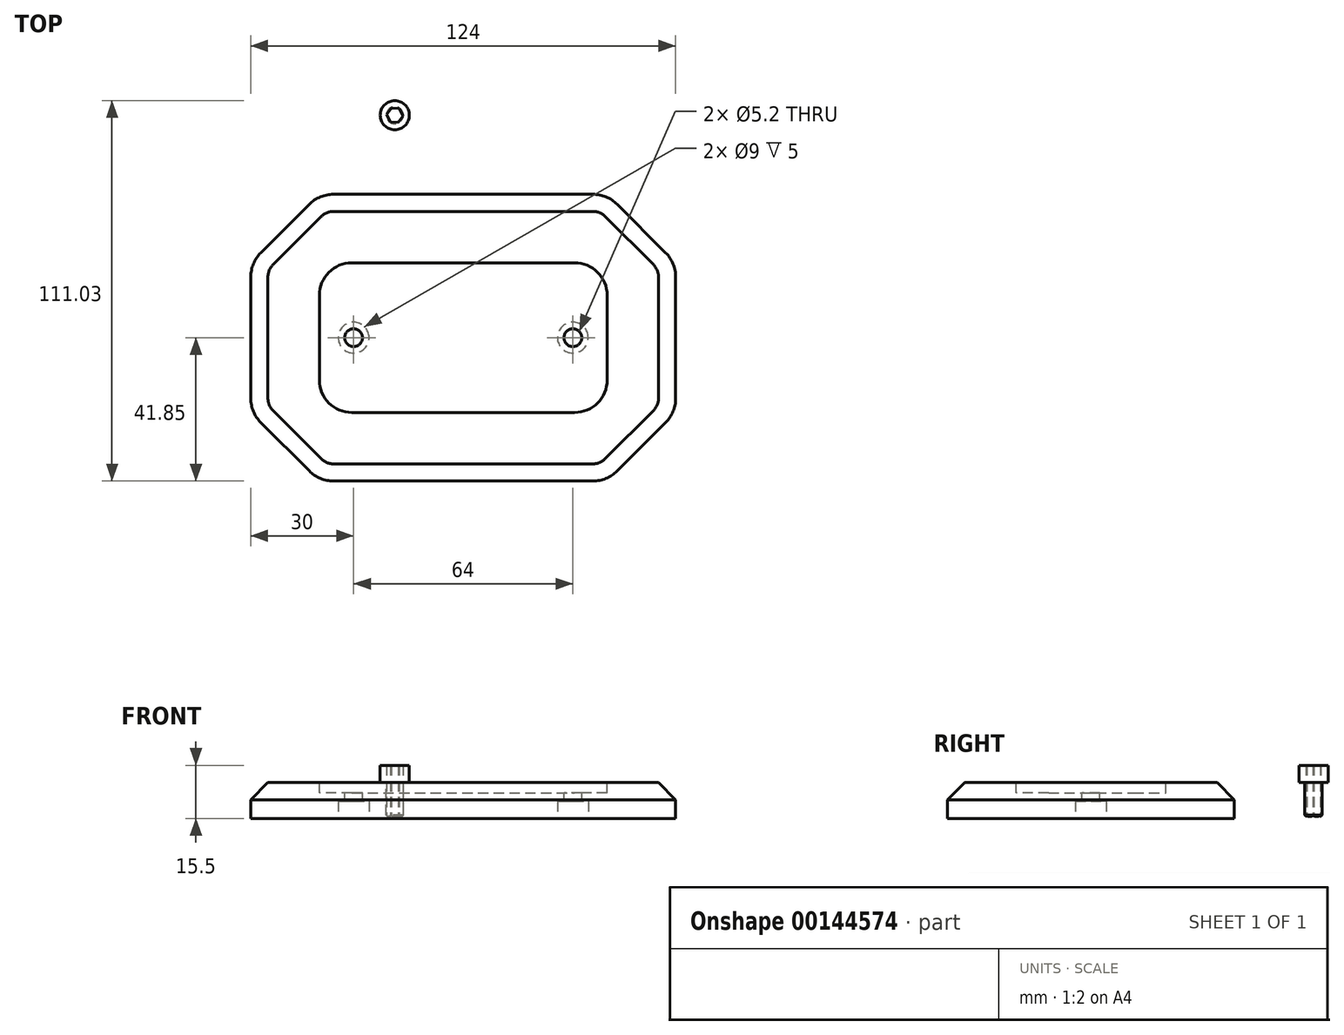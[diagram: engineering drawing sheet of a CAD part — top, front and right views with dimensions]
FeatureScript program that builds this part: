
annotation { "Feature Type Name" : "Feature", "Feature Type Description" : "" }
export const myFeature = defineFeature(function(context is Context, id is Id, definition is map)
    precondition{}
    {
        {
            var Q0;
            Q0=qCreatedBy(makeId("Top.planeOp"),FACE);
            var sketch = newSketch(context, id + "F0", { "sketchPlane" : qUnion([Q0])});
            skLineSegment(sketch, "E0.bottom", {"start": v(9.5, -43.7) * mm, "end": v(74.5, -43.7) * mm});
            skLineSegment(sketch, "E0.top", {"start": v(9.5, 0) * mm, "end": v(74.5, 0) * mm});
            skLineSegment(sketch, "E0.left", {"start": v(0, -34.2) * mm, "end": v(0, -9.5) * mm});
            skLineSegment(sketch, "E0.right", {"start": v(84, -34.2) * mm, "end": v(84, -9.5) * mm});
            skPoint(sketch, "E1.visualSharp", {"position": v(0, 0) * mm});
            skArc(sketch, "E1.filletArc", {"start": v(9.5, 0) * mm, "mid": v(2.78, -2.78) * mm, "end": v(0, -9.5) * mm});
            skPoint(sketch, "E2.visualSharp", {"position": v(84, 0) * mm});
            skArc(sketch, "E2.filletArc", {"start": v(84, -9.5) * mm, "mid": v(81.22, -2.78) * mm, "end": v(74.5, 0) * mm});
            skPoint(sketch, "E3.visualSharp", {"position": v(84, -43.7) * mm});
            skArc(sketch, "E3.filletArc", {"start": v(74.5, -43.7) * mm, "mid": v(81.22, -40.92) * mm, "end": v(84, -34.2) * mm});
            skPoint(sketch, "E4.visualSharp", {"position": v(0, -43.7) * mm});
            skArc(sketch, "E4.filletArc", {"start": v(0, -34.2) * mm, "mid": v(2.78, -40.92) * mm, "end": v(9.5, -43.7) * mm});
            skLineSegment(sketch, "E5.bottom", {"start": v(-20, 20) * mm, "end": v(104, 20) * mm, "construction": true});
            skLineSegment(sketch, "E5.top", {"start": v(-20, -63.7) * mm, "end": v(104, -63.7) * mm, "construction": true});
            skLineSegment(sketch, "E5.left", {"start": v(-20, 20) * mm, "end": v(-20, -63.7) * mm, "construction": true});
            skLineSegment(sketch, "E5.right", {"start": v(104, 20) * mm, "end": v(104, -63.7) * mm, "construction": true});
            skLineSegment(sketch, "E6", {"start": v(0, 20) * mm, "end": v(84, 20) * mm});
            skLineSegment(sketch, "E7", {"start": v(-20, 0) * mm, "end": v(-20, -43.7) * mm});
            skLineSegment(sketch, "E8", {"start": v(-20, 0) * mm, "end": v(0, 20) * mm});
            skLineSegment(sketch, "E9", {"start": v(84, 20) * mm, "end": v(104, 0) * mm});
            skLineSegment(sketch, "E10", {"start": v(104, 0) * mm, "end": v(104, -43.7) * mm});
            skLineSegment(sketch, "E11", {"start": v(104, -43.7) * mm, "end": v(84, -63.7) * mm});
            skLineSegment(sketch, "E12", {"start": v(84, -63.7) * mm, "end": v(0, -63.7) * mm});
            skLineSegment(sketch, "E13", {"start": v(0, -63.7) * mm, "end": v(-20, -43.7) * mm});
            skCircle(sketch, "E14", {"center": v(74, -21.85) * mm, "radius": 2.6 * mm});
            skLineSegment(sketch, "E15", {"start": v(84, -21.85) * mm, "end": v(0, -21.85) * mm, "construction": true});
            skCircle(sketch, "E16", {"center": v(10, -21.85) * mm, "radius": 2.6 * mm});
            skCircle(sketch, "E17", {"center": v(22.02, 43.08) * mm, "radius": 4.25 * mm});
            skCircle(sketch, "E18", {"center": v(22.02, 43.08) * mm, "radius": 2.5 * mm});
            skCircle(sketch, "E19.cCircle", {"center": v(22.02, 43.08) * mm, "radius": 2.07 * mm, "construction": true});
            skLineSegment(sketch, "E19.0", {"start": v(23.34, 45.06) * mm, "end": v(24.4, 42.92) * mm});
            skLineSegment(sketch, "E19.1", {"start": v(24.4, 42.92) * mm, "end": v(23.07, 40.94) * mm});
            skLineSegment(sketch, "E19.2", {"start": v(23.07, 40.94) * mm, "end": v(20.7, 41.1) * mm});
            skLineSegment(sketch, "E19.3", {"start": v(20.7, 41.1) * mm, "end": v(19.64, 43.23) * mm});
            skLineSegment(sketch, "E19.4", {"start": v(19.64, 43.23) * mm, "end": v(20.96, 45.22) * mm});
            skLineSegment(sketch, "E19.5", {"start": v(20.96, 45.22) * mm, "end": v(23.34, 45.06) * mm});
            skPoint(sketch, "E19.0.midPoint", {"position": v(23.87, 44) * mm});
            skSolve(sketch);
        }
        {
            var Q0;
            Q0=makeQuery(id+"F0.imprint","IMPRINT",FACE,{"disambiguationData":[TD([[makeQuery(id+"F0.imprint","IMPRINT",EDGE,{"derivedFrom":sQuery(id+"F0.wireOp",EDGE,"E0.bottom")}),1.0]])]});
            var Q1;
            Q1=makeQuery(id+"F0.imprint","IMPRINT",FACE,{"disambiguationData":[TD([[makeQuery(id+"F0.imprint","IMPRINT",EDGE,{"derivedFrom":sQuery(id+"F0.wireOp",EDGE,"E0.bottom")}),-1.0]])]});
            extrude(context, id + "F1", {"entities" : qUnion([Q0, Q1]), "oppositeDirection" : true, "depth" : 10.5 * mm});
        }
        {
            var Q0;
            Q0=makeQuery(id+"F0.imprint","IMPRINT",FACE,{"disambiguationData":[TD([[makeQuery(id+"F0.imprint","IMPRINT",EDGE,{"derivedFrom":sQuery(id+"F0.wireOp",EDGE,"E0.bottom")}),1.0]])]});
            extrude(context, id + "F2", {"entities" : qUnion([Q0]), "operationType" : NewBodyOperationType.REMOVE, "oppositeDirection" : true, "depth" : 3 * mm});
        }
        {
            var Q0;
            Q0=makeQuery(id+"F1.opExtrude","SWEPT_EDGE",EDGE,{"disambiguationData":[OSD([sQuery(id+"F0.wireOp",EDGE,"E6"),sQuery(id+"F0.wireOp",EDGE,"E8")])]});
            var Q1;
            Q1=makeQuery(id+"F1.opExtrude","SWEPT_EDGE",EDGE,{"disambiguationData":[OSD([sQuery(id+"F0.wireOp",EDGE,"E7"),sQuery(id+"F0.wireOp",EDGE,"E8")])]});
            var Q2;
            Q2=makeQuery(id+"F1.opExtrude","SWEPT_EDGE",EDGE,{"disambiguationData":[OSD([sQuery(id+"F0.wireOp",EDGE,"E7"),sQuery(id+"F0.wireOp",EDGE,"E13")])]});
            var Q3;
            Q3=makeQuery(id+"F1.opExtrude","SWEPT_EDGE",EDGE,{"disambiguationData":[OSD([sQuery(id+"F0.wireOp",EDGE,"E12"),sQuery(id+"F0.wireOp",EDGE,"E13")])]});
            var Q4;
            Q4=makeQuery(id+"F1.opExtrude","SWEPT_EDGE",EDGE,{"disambiguationData":[OSD([sQuery(id+"F0.wireOp",EDGE,"E11"),sQuery(id+"F0.wireOp",EDGE,"E12")])]});
            var Q5;
            Q5=makeQuery(id+"F1.opExtrude","SWEPT_EDGE",EDGE,{"disambiguationData":[OSD([sQuery(id+"F0.wireOp",EDGE,"E10"),sQuery(id+"F0.wireOp",EDGE,"E11")])]});
            var Q6;
            Q6=makeQuery(id+"F1.opExtrude","SWEPT_EDGE",EDGE,{"disambiguationData":[OSD([sQuery(id+"F0.wireOp",EDGE,"E9"),sQuery(id+"F0.wireOp",EDGE,"E10")])]});
            var Q7;
            Q7=makeQuery(id+"F1.opExtrude","SWEPT_EDGE",EDGE,{"disambiguationData":[OSD([sQuery(id+"F0.wireOp",EDGE,"E6"),sQuery(id+"F0.wireOp",EDGE,"E9")])]});
            fillet(context, id + "F3", {"entities" : qUnion([Q0, Q1, Q2, Q3, Q4, Q5, Q6, Q7]), "radius" : 10 * mm, "tangentPropagation" : true, "allowEdgeOverflow" : false});
        }
        {
            var Q0;
            Q0=makeQuery(id+"F1.opExtrude","CAP_EDGE",EDGE,{"disambiguationData":[OSD([sQuery(id+"F0.wireOp",EDGE,"E12")])],"isStart":true});
            chamfer(context, id + "F4", {"entities" : qUnion([Q0]), "width" : 5 * mm, "tangentPropagation" : true});
        }
        {
            var Q0;
            Q0=makeQuery(id+"F1.opExtrude","CAP_FACE",FACE,{"disambiguationData":[OSD([sQuery(id+"F0.wireOp",EDGE,"E6"),sQuery(id+"F0.wireOp",EDGE,"E7"),sQuery(id+"F0.wireOp",EDGE,"E8"),sQuery(id+"F0.wireOp",EDGE,"E9"),sQuery(id+"F0.wireOp",EDGE,"E10"),sQuery(id+"F0.wireOp",EDGE,"E11"),sQuery(id+"F0.wireOp",EDGE,"E12"),sQuery(id+"F0.wireOp",EDGE,"E13"),sQuery(id+"F0.wireOp",EDGE,"E14"),sQuery(id+"F0.wireOp",EDGE,"E16")])],"isStart":false});
            var sketch = newSketch(context, id + "F5", { "sketchPlane" : qUnion([Q0])});
            skPoint(sketch, "E20.0", {"position": v(74, 21.85) * mm});
            skPoint(sketch, "E21.0", {"position": v(10, 21.85) * mm});
            skCircle(sketch, "E22", {"center": v(74, 21.85) * mm, "radius": 4.5 * mm});
            skCircle(sketch, "E23", {"center": v(10, 21.85) * mm, "radius": 4.5 * mm});
            skSolve(sketch);
        }
        {
            var Q0;
            Q0 = qSketchRegion(id + "F5", true);
            extrude(context, id + "F6", {"entities" : qUnion([Q0]), "operationType" : NewBodyOperationType.REMOVE, "oppositeDirection" : true, "depth" : 5 * mm});
        }
        {
            var Q0;
            Q0=makeQuery(id+"F0.imprint","IMPRINT",FACE,{"disambiguationData":[TD([[makeQuery(id+"F0.imprint","IMPRINT",EDGE,{"derivedFrom":sQuery(id+"F0.wireOp",EDGE,"E17")}),1.0]])]});
            var Q1;
            Q1=makeQuery(id+"F0.imprint","IMPRINT",FACE,{"disambiguationData":[TD([[makeQuery(id+"F0.imprint","IMPRINT",EDGE,{"derivedFrom":sQuery(id+"F0.wireOp",EDGE,"E18")}),1.0]])]});
            extrude(context, id + "F7", {"entities" : qUnion([Q0, Q1]), "depth" : 5 * mm});
        }
        {
            var Q0;
            Q0=makeQuery(id+"F0.imprint","IMPRINT",FACE,{"disambiguationData":[TD([[makeQuery(id+"F0.imprint","IMPRINT",EDGE,{"derivedFrom":sQuery(id+"F0.wireOp",EDGE,"E18")}),1.0]])]});
            extrude(context, id + "F8", {"entities" : qUnion([Q0]), "operationType" : NewBodyOperationType.ADD, "oppositeDirection" : true, "depth" : 10 * mm});
        }
        {
            var Q0;
            Q0=makeQuery(id+"F8.opExtrude","CAP_EDGE",EDGE,{"disambiguationData":[OSD([sQuery(id+"F0.wireOp",EDGE,"E18")])],"isStart":false});
            chamfer(context, id + "F9", {"entities" : qUnion([Q0]), "width" : 0.5 * mm, "tangentPropagation" : true});
        }
    });
